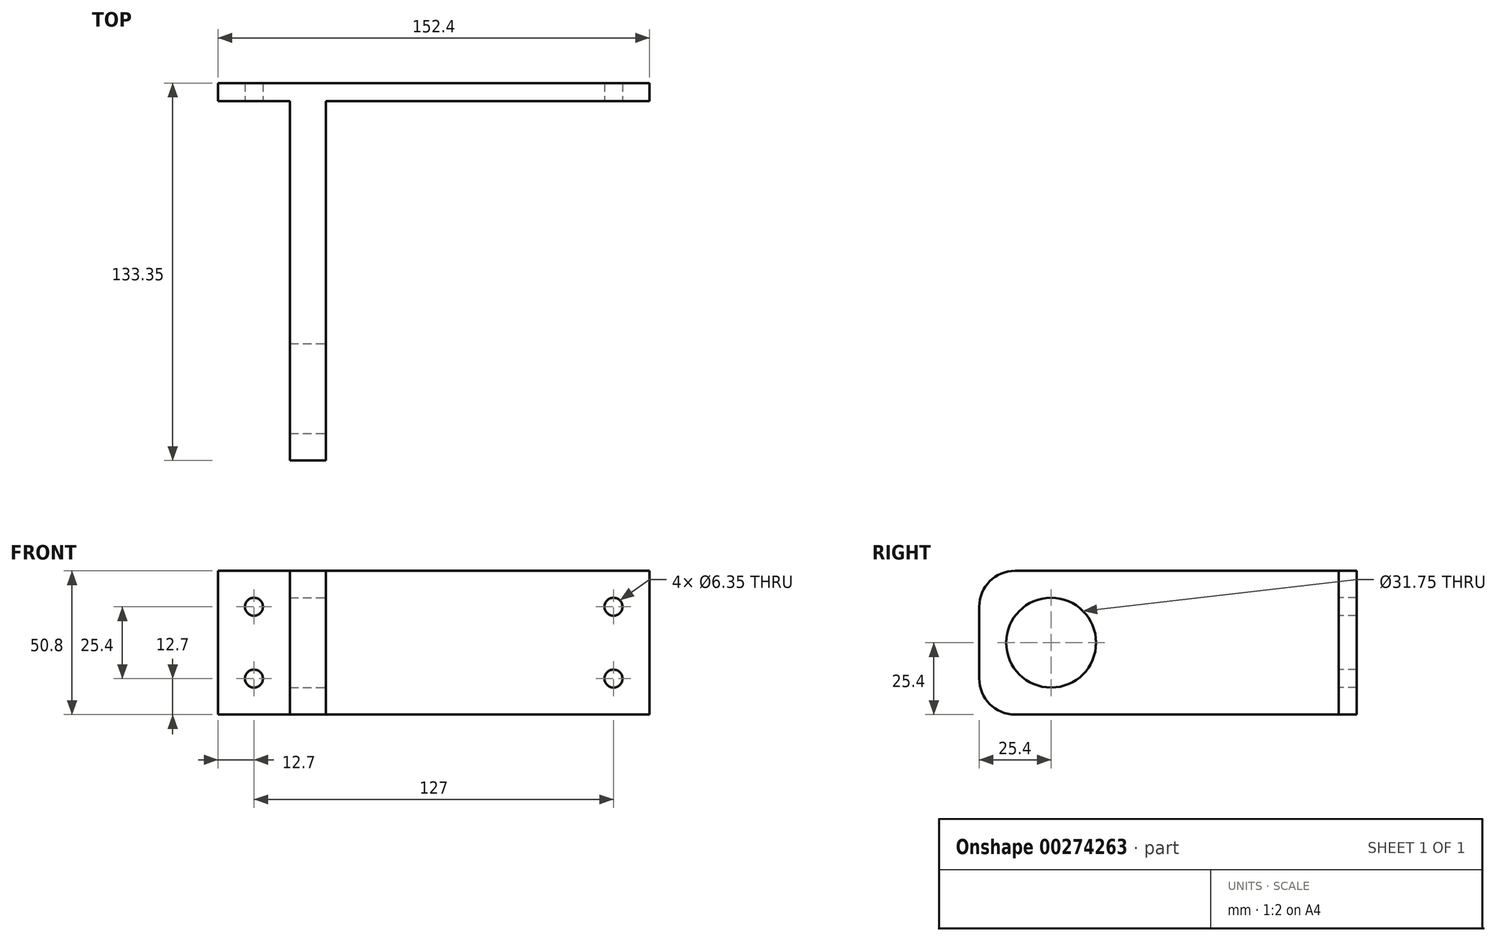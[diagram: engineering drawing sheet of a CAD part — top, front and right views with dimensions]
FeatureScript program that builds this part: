
annotation { "Feature Type Name" : "Feature", "Feature Type Description" : "" }
export const myFeature = defineFeature(function(context is Context, id is Id, definition is map)
    precondition{}
    {
        {
            var Q0;
            Q0=qCreatedBy(makeId("Front.planeOp"),FACE);
            var sketch = newSketch(context, id + "F0", { "sketchPlane" : qUnion([Q0])});
            skLineSegment(sketch, "E0.bottom", {"start": v(0, 0) * mm, "end": v(152.4, 0) * mm});
            skLineSegment(sketch, "E0.top", {"start": v(0, 50.8) * mm, "end": v(152.4, 50.8) * mm});
            skLineSegment(sketch, "E0.left", {"start": v(0, 0) * mm, "end": v(0, 50.8) * mm});
            skLineSegment(sketch, "E0.right", {"start": v(152.4, 0) * mm, "end": v(152.4, 50.8) * mm});
            skSolve(sketch);
        }
        {
            var Q0;
            Q0=makeQuery(id+"F0.imprint","IMPRINT",FACE,{"disambiguationData":[TD([[makeQuery(id+"F0.imprint","IMPRINT",EDGE,{"derivedFrom":sQuery(id+"F0.wireOp",EDGE,"E0.bottom")}),1.0]])]});
            extrude(context, id + "F1", {"entities" : qUnion([Q0]), "depth" : 6.35 * mm});
        }
        {
            var Q0;
            Q0=makeQuery(id+"F1.opExtrude","CAP_FACE",FACE,{"disambiguationData":[OSD([sQuery(id+"F0.wireOp",EDGE,"E0.bottom"),sQuery(id+"F0.wireOp",EDGE,"E0.top"),sQuery(id+"F0.wireOp",EDGE,"E0.left"),sQuery(id+"F0.wireOp",EDGE,"E0.right")])],"isStart":false});
            var sketch = newSketch(context, id + "F2", { "sketchPlane" : qUnion([Q0])});
            skPoint(sketch, "E1", {"position": v(12.7, 38.1) * mm});
            skPoint(sketch, "E2", {"position": v(12.7, 12.7) * mm});
            skPoint(sketch, "E3", {"position": v(139.7, 38.1) * mm});
            skPoint(sketch, "E4", {"position": v(139.7, 12.7) * mm});
            skSolve(sketch);
        }
        {
            var Q0;
            Q0=sQuery(id+"F2.wireOp",VERTEX,"E1");
            var Q1;
            Q1=sQuery(id+"F2.wireOp",VERTEX,"E2");
            var Q2;
            Q2=sQuery(id+"F2.wireOp",VERTEX,"E3");
            var Q3;
            Q3=sQuery(id+"F2.wireOp",VERTEX,"E4");
            var Q4;
            Q4=makeQuery(id+"F1.opExtrude","SWEPT_BODY",BODY,{"disambiguationData":[OSD([sQuery(id+"F0.wireOp",EDGE,"E0.bottom"),sQuery(id+"F0.wireOp",EDGE,"E0.top"),sQuery(id+"F0.wireOp",EDGE,"E0.left"),sQuery(id+"F0.wireOp",EDGE,"E0.right")])]});
            hole(context, id + "F3", {"style" : HoleStyle.SIMPLE, "endStyle" : HoleEndStyle.THROUGH, "holeDiameter" : 6.35 * mm, "tappedDepth" : 12.7 * mm, "tapClearance" : 3, "locations" : qUnion([Q0, Q1, Q2, Q3]), "scope" : qUnion([Q4])});
        }
        {
            var Q0;
            Q0=makeQuery(id+"F1.opExtrude","CAP_FACE",FACE,{"disambiguationData":[OSD([sQuery(id+"F0.wireOp",EDGE,"E0.bottom"),sQuery(id+"F0.wireOp",EDGE,"E0.top"),sQuery(id+"F0.wireOp",EDGE,"E0.left"),sQuery(id+"F0.wireOp",EDGE,"E0.right")])],"isStart":false});
            var sketch = newSketch(context, id + "F4", { "sketchPlane" : qUnion([Q0])});
            skLineSegment(sketch, "E5.bottom", {"start": v(25.4, 50.8) * mm, "end": v(38.1, 50.8) * mm});
            skLineSegment(sketch, "E5.top", {"start": v(25.4, 0) * mm, "end": v(38.1, 0) * mm});
            skLineSegment(sketch, "E5.left", {"start": v(25.4, 50.8) * mm, "end": v(25.4, 0) * mm});
            skLineSegment(sketch, "E5.right", {"start": v(38.1, 50.8) * mm, "end": v(38.1, 0) * mm});
            skSolve(sketch);
        }
        {
            var Q0;
            Q0=makeQuery(id+"F4.imprint","IMPRINT",FACE,{"disambiguationData":[TD([[makeQuery(id+"F4.imprint","IMPRINT",EDGE,{"derivedFrom":sQuery(id+"F4.wireOp",EDGE,"E5.bottom")}),-1.0]])]});
            extrude(context, id + "F5", {"entities" : qUnion([Q0]), "operationType" : NewBodyOperationType.ADD, "depth" : 127 * mm});
        }
        {
            var Q0;
            Q0=makeQuery(id+"F5.opExtrude","CAP_EDGE",EDGE,{"disambiguationData":[OSD([sQuery(id+"F4.wireOp",EDGE,"E5.top")])],"isStart":false});
            var Q1;
            Q1=makeQuery(id+"F5.opExtrude","CAP_EDGE",EDGE,{"disambiguationData":[OSD([sQuery(id+"F4.wireOp",EDGE,"E5.bottom")])],"isStart":false});
            fillet(context, id + "F6", {"entities" : qUnion([Q0, Q1]), "radius" : 12.7 * mm, "tangentPropagation" : true, "allowEdgeOverflow" : false});
        }
        {
            var Q0;
            Q0=makeQuery(id+"F5.opExtrude","SWEPT_FACE",FACE,{"disambiguationData":[OSD([sQuery(id+"F4.wireOp",EDGE,"E5.right")])]});
            var sketch = newSketch(context, id + "F7", { "sketchPlane" : qUnion([Q0])});
            skPoint(sketch, "E6", {"position": v(-107.95, 25.4) * mm});
            skSolve(sketch);
        }
        {
            var Q0;
            Q0=sQuery(id+"F7.wireOp",VERTEX,"E6");
            var Q1;
            Q1=makeQuery(id+"F1.opExtrude","SWEPT_BODY",BODY,{"disambiguationData":[OSD([sQuery(id+"F0.wireOp",EDGE,"E0.bottom"),sQuery(id+"F0.wireOp",EDGE,"E0.top"),sQuery(id+"F0.wireOp",EDGE,"E0.left"),sQuery(id+"F0.wireOp",EDGE,"E0.right")])]});
            hole(context, id + "F8", {"style" : HoleStyle.SIMPLE, "endStyle" : HoleEndStyle.THROUGH, "holeDiameter" : 31.75 * mm, "tappedDepth" : 12.7 * mm, "tapClearance" : 3, "locations" : qUnion([Q0]), "scope" : qUnion([Q1])});
        }
    });
